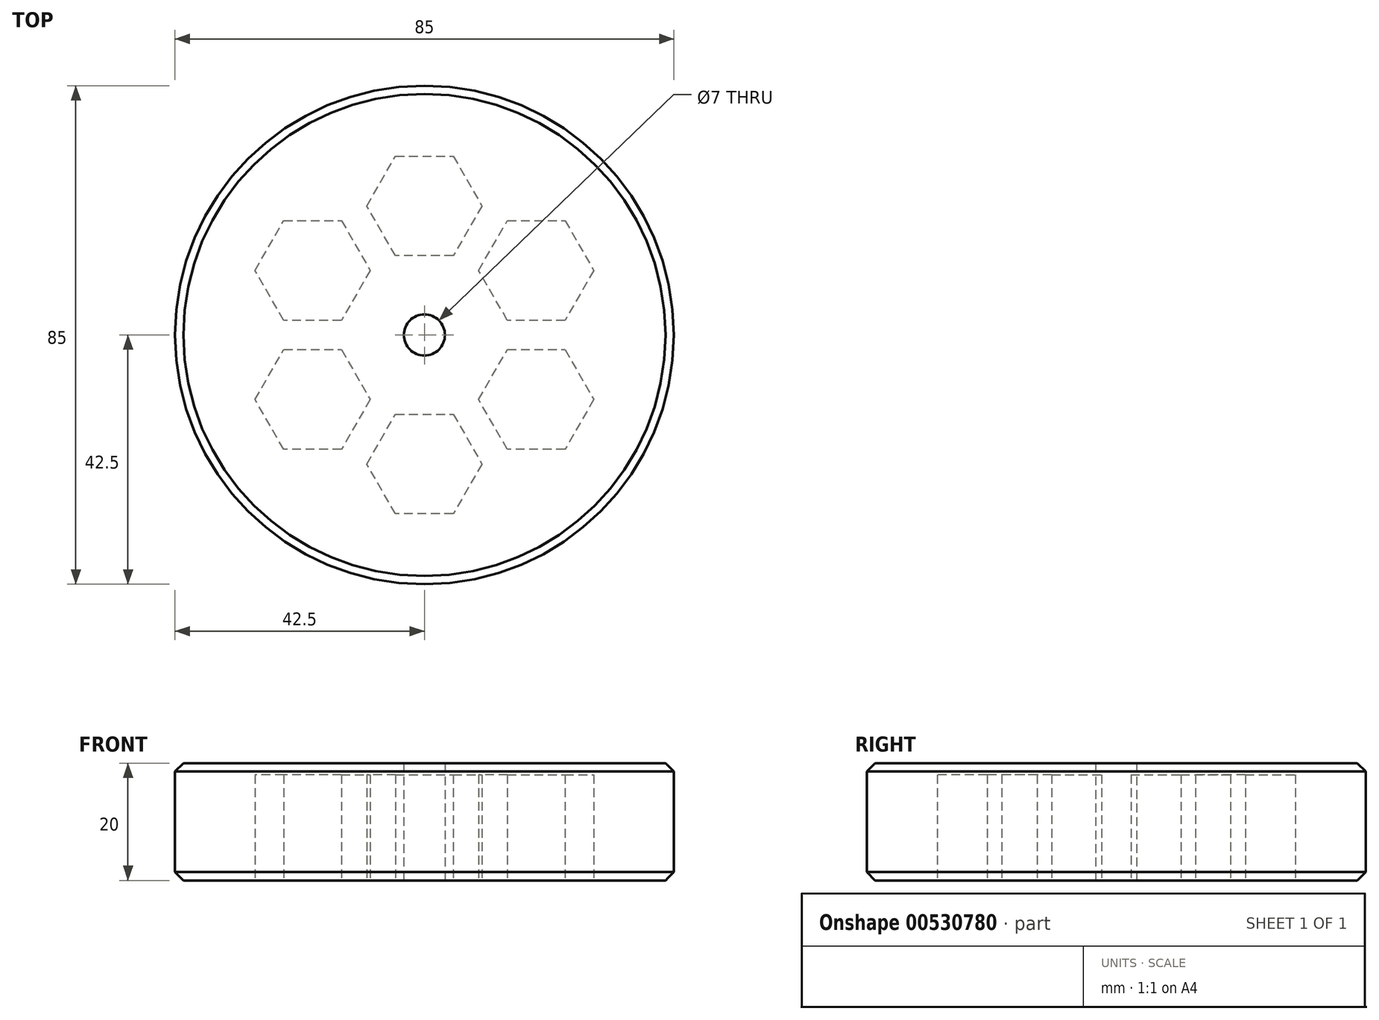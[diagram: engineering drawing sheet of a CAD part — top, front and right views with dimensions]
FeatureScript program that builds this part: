
annotation { "Feature Type Name" : "Feature", "Feature Type Description" : "" }
export const myFeature = defineFeature(function(context is Context, id is Id, definition is map)
    precondition{}
    {
        {
            var Q0;
            Q0=qCreatedBy(makeId("Top.planeOp"),FACE);
            var sketch = newSketch(context, id + "F0", { "sketchPlane" : qUnion([Q0])});
            skCircle(sketch, "E0", {"center": v(0, 0) * mm, "radius": 42.5 * mm});
            skCircle(sketch, "E1.cCircle", {"center": v(0, 22) * mm, "radius": 8.5 * mm, "construction": true});
            skLineSegment(sketch, "E1.0", {"start": v(4.9, 13.5) * mm, "end": v(-4.9, 13.5) * mm});
            skLineSegment(sketch, "E1.1", {"start": v(-4.9, 13.5) * mm, "end": v(-9.81, 22) * mm});
            skLineSegment(sketch, "E1.2", {"start": v(-9.81, 22) * mm, "end": v(-4.9, 30.5) * mm});
            skLineSegment(sketch, "E1.3", {"start": v(-4.9, 30.5) * mm, "end": v(4.9, 30.5) * mm});
            skLineSegment(sketch, "E1.4", {"start": v(4.9, 30.5) * mm, "end": v(9.81, 22) * mm});
            skLineSegment(sketch, "E1.5", {"start": v(9.81, 22) * mm, "end": v(4.9, 13.5) * mm});
            skPoint(sketch, "E1.0.midPoint", {"position": v(0, 13.5) * mm});
            skLineSegment(sketch, "E2.1.0", {"start": v(-14.15, 2.5) * mm, "end": v(-23.96, 2.5) * mm});
            skLineSegment(sketch, "E2.1.1", {"start": v(-23.96, 2.5) * mm, "end": v(-28.87, 11) * mm});
            skLineSegment(sketch, "E2.1.2", {"start": v(-28.87, 11) * mm, "end": v(-23.96, 19.5) * mm});
            skLineSegment(sketch, "E2.1.3", {"start": v(-23.96, 19.5) * mm, "end": v(-14.15, 19.5) * mm});
            skLineSegment(sketch, "E2.1.4", {"start": v(-14.15, 19.5) * mm, "end": v(-9.24, 11) * mm});
            skLineSegment(sketch, "E2.1.5", {"start": v(-9.24, 11) * mm, "end": v(-14.15, 2.5) * mm});
            skLineSegment(sketch, "E2.2.0", {"start": v(-9.24, -11) * mm, "end": v(-14.15, -19.5) * mm});
            skLineSegment(sketch, "E2.2.1", {"start": v(-14.15, -19.5) * mm, "end": v(-23.96, -19.5) * mm});
            skLineSegment(sketch, "E2.2.2", {"start": v(-23.96, -19.5) * mm, "end": v(-28.87, -11) * mm});
            skLineSegment(sketch, "E2.2.3", {"start": v(-28.87, -11) * mm, "end": v(-23.96, -2.5) * mm});
            skLineSegment(sketch, "E2.2.4", {"start": v(-23.96, -2.5) * mm, "end": v(-14.15, -2.5) * mm});
            skLineSegment(sketch, "E2.2.5", {"start": v(-14.15, -2.5) * mm, "end": v(-9.24, -11) * mm});
            skLineSegment(sketch, "E2.3.0", {"start": v(4.9, -13.5) * mm, "end": v(9.81, -22) * mm});
            skLineSegment(sketch, "E2.3.1", {"start": v(9.81, -22) * mm, "end": v(4.9, -30.5) * mm});
            skLineSegment(sketch, "E2.3.2", {"start": v(4.9, -30.5) * mm, "end": v(-4.9, -30.5) * mm});
            skLineSegment(sketch, "E2.3.3", {"start": v(-4.9, -30.5) * mm, "end": v(-9.81, -22) * mm});
            skLineSegment(sketch, "E2.3.4", {"start": v(-9.81, -22) * mm, "end": v(-4.9, -13.5) * mm});
            skLineSegment(sketch, "E2.3.5", {"start": v(-4.9, -13.5) * mm, "end": v(4.9, -13.5) * mm});
            skLineSegment(sketch, "E2.4.0", {"start": v(14.15, -2.5) * mm, "end": v(23.96, -2.5) * mm});
            skLineSegment(sketch, "E2.4.1", {"start": v(23.96, -2.5) * mm, "end": v(28.87, -11) * mm});
            skLineSegment(sketch, "E2.4.2", {"start": v(28.87, -11) * mm, "end": v(23.96, -19.5) * mm});
            skLineSegment(sketch, "E2.4.3", {"start": v(23.96, -19.5) * mm, "end": v(14.15, -19.5) * mm});
            skLineSegment(sketch, "E2.4.4", {"start": v(14.15, -19.5) * mm, "end": v(9.24, -11) * mm});
            skLineSegment(sketch, "E2.4.5", {"start": v(9.24, -11) * mm, "end": v(14.15, -2.5) * mm});
            skLineSegment(sketch, "E2.5.0", {"start": v(9.24, 11) * mm, "end": v(14.15, 19.5) * mm});
            skLineSegment(sketch, "E2.5.1", {"start": v(14.15, 19.5) * mm, "end": v(23.96, 19.5) * mm});
            skLineSegment(sketch, "E2.5.2", {"start": v(23.96, 19.5) * mm, "end": v(28.87, 11) * mm});
            skLineSegment(sketch, "E2.5.3", {"start": v(28.87, 11) * mm, "end": v(23.96, 2.5) * mm});
            skLineSegment(sketch, "E2.5.4", {"start": v(23.96, 2.5) * mm, "end": v(14.15, 2.5) * mm});
            skLineSegment(sketch, "E2.5.5", {"start": v(14.15, 2.5) * mm, "end": v(9.24, 11) * mm});
            skCircle(sketch, "E3", {"center": v(0, 0) * mm, "radius": 3.5 * mm});
            skSolve(sketch);
        }
        {
            var Q0;
            Q0=makeQuery(id+"F0.imprint","IMPRINT",FACE,{"disambiguationData":[TD([[makeQuery(id+"F0.imprint","IMPRINT",EDGE,{"derivedFrom":sQuery(id+"F0.wireOp",EDGE,"E0")}),1.0]])]});
            extrude(context, id + "F1", {"entities" : qUnion([Q0]), "depth" : 20 * mm, "offsetDistance" : 25 * mm});
        }
        {
            var Q0;
            Q0=makeQuery(id+"F0.imprint","IMPRINT",FACE,{"disambiguationData":[TD([[makeQuery(id+"F0.imprint","IMPRINT",EDGE,{"derivedFrom":sQuery(id+"F0.wireOp",EDGE,"E2.1.0")}),-1.0]])]});
            var Q1;
            Q1=makeQuery(id+"F0.imprint","IMPRINT",FACE,{"disambiguationData":[TD([[makeQuery(id+"F0.imprint","IMPRINT",EDGE,{"derivedFrom":sQuery(id+"F0.wireOp",EDGE,"E1.0")}),-1.0]])]});
            var Q2;
            Q2=makeQuery(id+"F0.imprint","IMPRINT",FACE,{"disambiguationData":[TD([[makeQuery(id+"F0.imprint","IMPRINT",EDGE,{"derivedFrom":sQuery(id+"F0.wireOp",EDGE,"E2.5.0")}),-1.0]])]});
            var Q3;
            Q3=makeQuery(id+"F0.imprint","IMPRINT",FACE,{"disambiguationData":[TD([[makeQuery(id+"F0.imprint","IMPRINT",EDGE,{"derivedFrom":sQuery(id+"F0.wireOp",EDGE,"E2.4.0")}),-1.0]])]});
            var Q4;
            Q4=makeQuery(id+"F0.imprint","IMPRINT",FACE,{"disambiguationData":[TD([[makeQuery(id+"F0.imprint","IMPRINT",EDGE,{"derivedFrom":sQuery(id+"F0.wireOp",EDGE,"E2.3.0")}),-1.0]])]});
            var Q5;
            Q5=makeQuery(id+"F0.imprint","IMPRINT",FACE,{"disambiguationData":[TD([[makeQuery(id+"F0.imprint","IMPRINT",EDGE,{"derivedFrom":sQuery(id+"F0.wireOp",EDGE,"E2.2.0")}),-1.0]])]});
            var Q6;
            Q6=makeQuery(id+"F1.opExtrude","CAP_FACE",FACE,{"disambiguationData":[OSD([sQuery(id+"F0.wireOp",EDGE,"E0"),sQuery(id+"F0.wireOp",EDGE,"E1.0"),sQuery(id+"F0.wireOp",EDGE,"E1.1"),sQuery(id+"F0.wireOp",EDGE,"E1.2"),sQuery(id+"F0.wireOp",EDGE,"E1.3"),sQuery(id+"F0.wireOp",EDGE,"E1.4"),sQuery(id+"F0.wireOp",EDGE,"E1.5"),sQuery(id+"F0.wireOp",EDGE,"E2.1.0"),sQuery(id+"F0.wireOp",EDGE,"E2.1.1"),sQuery(id+"F0.wireOp",EDGE,"E2.1.2"),sQuery(id+"F0.wireOp",EDGE,"E2.1.3"),sQuery(id+"F0.wireOp",EDGE,"E2.1.4"),sQuery(id+"F0.wireOp",EDGE,"E2.1.5"),sQuery(id+"F0.wireOp",EDGE,"E2.2.0"),sQuery(id+"F0.wireOp",EDGE,"E2.2.1"),sQuery(id+"F0.wireOp",EDGE,"E2.2.2"),sQuery(id+"F0.wireOp",EDGE,"E2.2.3"),sQuery(id+"F0.wireOp",EDGE,"E2.2.4"),sQuery(id+"F0.wireOp",EDGE,"E2.2.5"),sQuery(id+"F0.wireOp",EDGE,"E2.3.0"),sQuery(id+"F0.wireOp",EDGE,"E2.3.1"),sQuery(id+"F0.wireOp",EDGE,"E2.3.2"),sQuery(id+"F0.wireOp",EDGE,"E2.3.3"),sQuery(id+"F0.wireOp",EDGE,"E2.3.4"),sQuery(id+"F0.wireOp",EDGE,"E2.3.5"),sQuery(id+"F0.wireOp",EDGE,"E2.4.0"),sQuery(id+"F0.wireOp",EDGE,"E2.4.1"),sQuery(id+"F0.wireOp",EDGE,"E2.4.2"),sQuery(id+"F0.wireOp",EDGE,"E2.4.3"),sQuery(id+"F0.wireOp",EDGE,"E2.4.4"),sQuery(id+"F0.wireOp",EDGE,"E2.4.5"),sQuery(id+"F0.wireOp",EDGE,"E2.5.0"),sQuery(id+"F0.wireOp",EDGE,"E2.5.1"),sQuery(id+"F0.wireOp",EDGE,"E2.5.2"),sQuery(id+"F0.wireOp",EDGE,"E2.5.3"),sQuery(id+"F0.wireOp",EDGE,"E2.5.4"),sQuery(id+"F0.wireOp",EDGE,"E2.5.5"),sQuery(id+"F0.wireOp",EDGE,"E3")])],"isStart":false});
            extrude(context, id + "F2", {"entities" : qUnion([Q0, Q1, Q2, Q3, Q4, Q5]), "operationType" : NewBodyOperationType.ADD, "endBound" : BoundingType.UP_TO_SURFACE, "depth" : 25 * mm, "endBoundEntityFace" : qUnion([Q6]), "offsetDistance" : 25 * mm, "hasSecondDirection" : true, "secondDirectionOppositeDirection" : false, "secondDirectionDepth" : 18 * mm});
        }
        {
            var Q0;
            Q0=makeQuery(id+"F1.opExtrude","CAP_EDGE",EDGE,{"disambiguationData":[OSD([sQuery(id+"F0.wireOp",EDGE,"E0")])],"isStart":false});
            chamfer(context, id + "F3", {"entities" : qUnion([Q0]), "width" : 1.41 * mm, "tangentPropagation" : true});
        }
        {
            var Q0;
            Q0=makeQuery(id+"F1.opExtrude","CAP_EDGE",EDGE,{"disambiguationData":[OSD([sQuery(id+"F0.wireOp",EDGE,"E0")])],"isStart":true});
            chamfer(context, id + "F4", {"entities" : qUnion([Q0]), "width" : 1.41 * mm, "tangentPropagation" : true});
        }
    });
